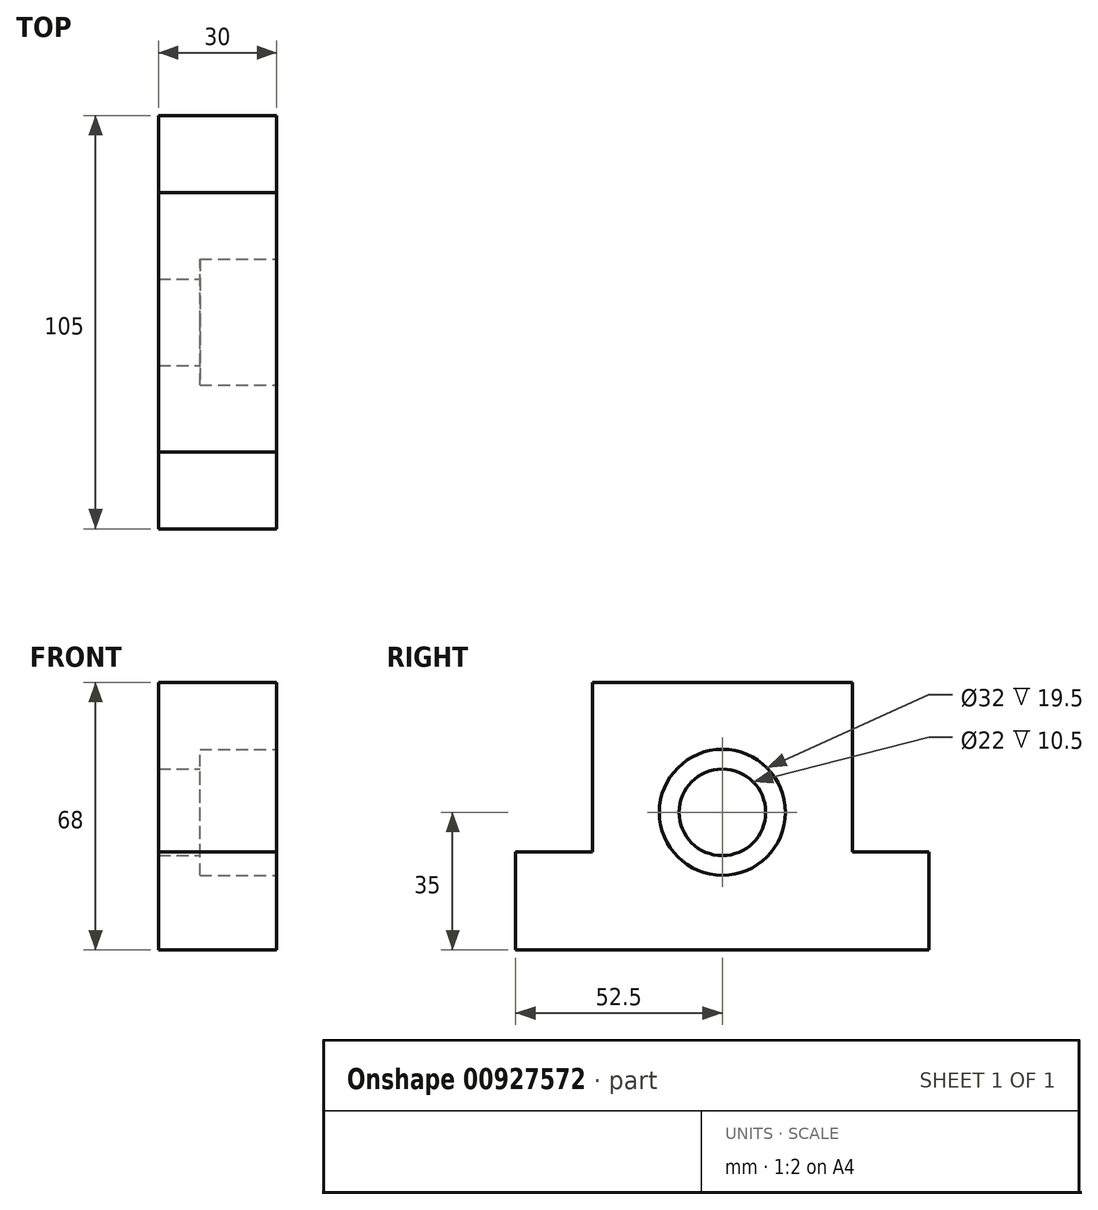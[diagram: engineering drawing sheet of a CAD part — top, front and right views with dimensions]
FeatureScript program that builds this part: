
annotation { "Feature Type Name" : "Feature", "Feature Type Description" : "" }
export const myFeature = defineFeature(function(context is Context, id is Id, definition is map)
    precondition{}
    {
        {
            var Q0;
            Q0=qCreatedBy(makeId("Right.planeOp"),FACE);
            var sketch = newSketch(context, id + "F0", { "sketchPlane" : qUnion([Q0])});
            skLineSegment(sketch, "E0.bottom", {"start": v(52.5, 34) * mm, "end": v(-52.5, 34) * mm});
            skLineSegment(sketch, "E0.top", {"start": v(52.5, -34) * mm, "end": v(-52.5, -34) * mm});
            skLineSegment(sketch, "E0.left", {"start": v(52.5, 34) * mm, "end": v(52.5, -34) * mm});
            skLineSegment(sketch, "E0.right", {"start": v(-52.5, 34) * mm, "end": v(-52.5, -34) * mm});
            skPoint(sketch, "E0.middle", {"position": v(0, 0) * mm});
            skSolve(sketch);
        }
        {
            var Q0;
            Q0 = qSketchRegion(id + "F0", true);
            extrude(context, id + "F1", {"entities" : qUnion([Q0]), "depth" : 30 * mm, "offsetDistance" : 25 * mm});
        }
        {
            var Q0;
            Q0=makeQuery(id+"F1.opExtrude","CAP_FACE",FACE,{"disambiguationData":[OSD([sQuery(id+"F0.wireOp",EDGE,"E0.bottom"),sQuery(id+"F0.wireOp",EDGE,"E0.top"),sQuery(id+"F0.wireOp",EDGE,"E0.left"),sQuery(id+"F0.wireOp",EDGE,"E0.right")])],"isStart":false});
            var sketch = newSketch(context, id + "F2", { "sketchPlane" : qUnion([Q0])});
            skLineSegment(sketch, "E1", {"start": v(-84.81, -9) * mm, "end": v(-33, -9) * mm});
            skLineSegment(sketch, "E2", {"start": v(-33, -9) * mm, "end": v(-33, 49.15) * mm});
            skLineSegment(sketch, "E3", {"start": v(0, 58.95) * mm, "end": v(0, -45.87) * mm, "construction": true});
            skLineSegment(sketch, "E4.MirrorCS", {"start": v(33, -9) * mm, "end": v(33, 49.15) * mm});
            skLineSegment(sketch, "E5.MirrorCS", {"start": v(84.81, -9) * mm, "end": v(33, -9) * mm});
            skSolve(sketch);
        }
        {
            var Q0;
            {var subQ0=sQuery(id+"F2.wireOp",EDGE,"E2");var subQ1=sQuery(id+"F2.wireOp",EDGE,"E1");var subQ2=makeQuery(id+"F2.imprint","INTERSECT",VERTEX,{"derivedFrom":[subQ1,subQ0]});Q0=makeQuery(id+"F2.imprint","IMPRINT",FACE,{"disambiguationData":[TD([[makeQuery(id+"F2.imprint","IMPRINT",EDGE,{"disambiguationData":[TD([[subQ2,1.0]])],"derivedFrom":subQ1}),1.0]])]});}
            var Q1;
            {var subQ0=sQuery(id+"F2.wireOp",EDGE,"E5.MirrorCS");var subQ1=sQuery(id+"F2.wireOp",EDGE,"E4.MirrorCS");var subQ2=makeQuery(id+"F2.imprint","INTERSECT",VERTEX,{"derivedFrom":[subQ1,subQ0]});Q1=makeQuery(id+"F2.imprint","IMPRINT",FACE,{"disambiguationData":[TD([[makeQuery(id+"F2.imprint","IMPRINT",EDGE,{"disambiguationData":[TD([[subQ2,-1.0]])],"derivedFrom":subQ1}),-1.0]])]});}
            extrude(context, id + "F3", {"entities" : qUnion([Q0, Q1]), "operationType" : NewBodyOperationType.REMOVE, "endBound" : BoundingType.THROUGH_ALL, "oppositeDirection" : true, "depth" : 25 * mm, "offsetDistance" : 25 * mm});
        }
        {
            var Q0;
            Q0=makeQuery(id+"F1.opExtrude","CAP_FACE",FACE,{"disambiguationData":[OSD([sQuery(id+"F0.wireOp",EDGE,"E0.bottom"),sQuery(id+"F0.wireOp",EDGE,"E0.top"),sQuery(id+"F0.wireOp",EDGE,"E0.left"),sQuery(id+"F0.wireOp",EDGE,"E0.right")])],"isStart":false});
            var sketch = newSketch(context, id + "F4", { "sketchPlane" : qUnion([Q0])});
            skLineSegment(sketch, "E6", {"start": v(-50.65, 1) * mm, "end": v(38.39, 1) * mm, "construction": true});
            skLineSegment(sketch, "E7", {"start": v(0, 53.95) * mm, "end": v(0, -47.91) * mm, "construction": true});
            skPoint(sketch, "E8", {"position": v(0, 1) * mm});
            skCircle(sketch, "E9", {"center": v(0, 1) * mm, "radius": 16 * mm});
            skCircle(sketch, "E10", {"center": v(0, 1) * mm, "radius": 11 * mm});
            skSolve(sketch);
        }
        {
            var Q0;
            Q0 = qSketchRegion(id + "F4", true);
            extrude(context, id + "F5", {"entities" : qUnion([Q0]), "operationType" : NewBodyOperationType.REMOVE, "oppositeDirection" : true, "depth" : 19.5 * mm, "offsetDistance" : 25 * mm});
        }
        {
            var Q0;
            Q0=makeQuery(id+"F5.boolean.opBoolean","SPLIT",FACE,{"disambiguationData":[TD([makeQuery(id+"F5.opExtrude","SWEPT_FACE",FACE,{"disambiguationData":[OSD([sQuery(id+"F4.wireOp",EDGE,"E10")])]})])],"derivedFrom":makeQuery(id+"F1.opExtrude","CAP_FACE",FACE,{"disambiguationData":[OSD([sQuery(id+"F0.wireOp",EDGE,"E0.bottom"),sQuery(id+"F0.wireOp",EDGE,"E0.top"),sQuery(id+"F0.wireOp",EDGE,"E0.left"),sQuery(id+"F0.wireOp",EDGE,"E0.right")])],"isStart":false})});
            extrude(context, id + "F6", {"entities" : qUnion([Q0]), "operationType" : NewBodyOperationType.REMOVE, "endBound" : BoundingType.THROUGH_ALL, "oppositeDirection" : true, "depth" : 25 * mm, "offsetDistance" : 25 * mm});
        }
    });
